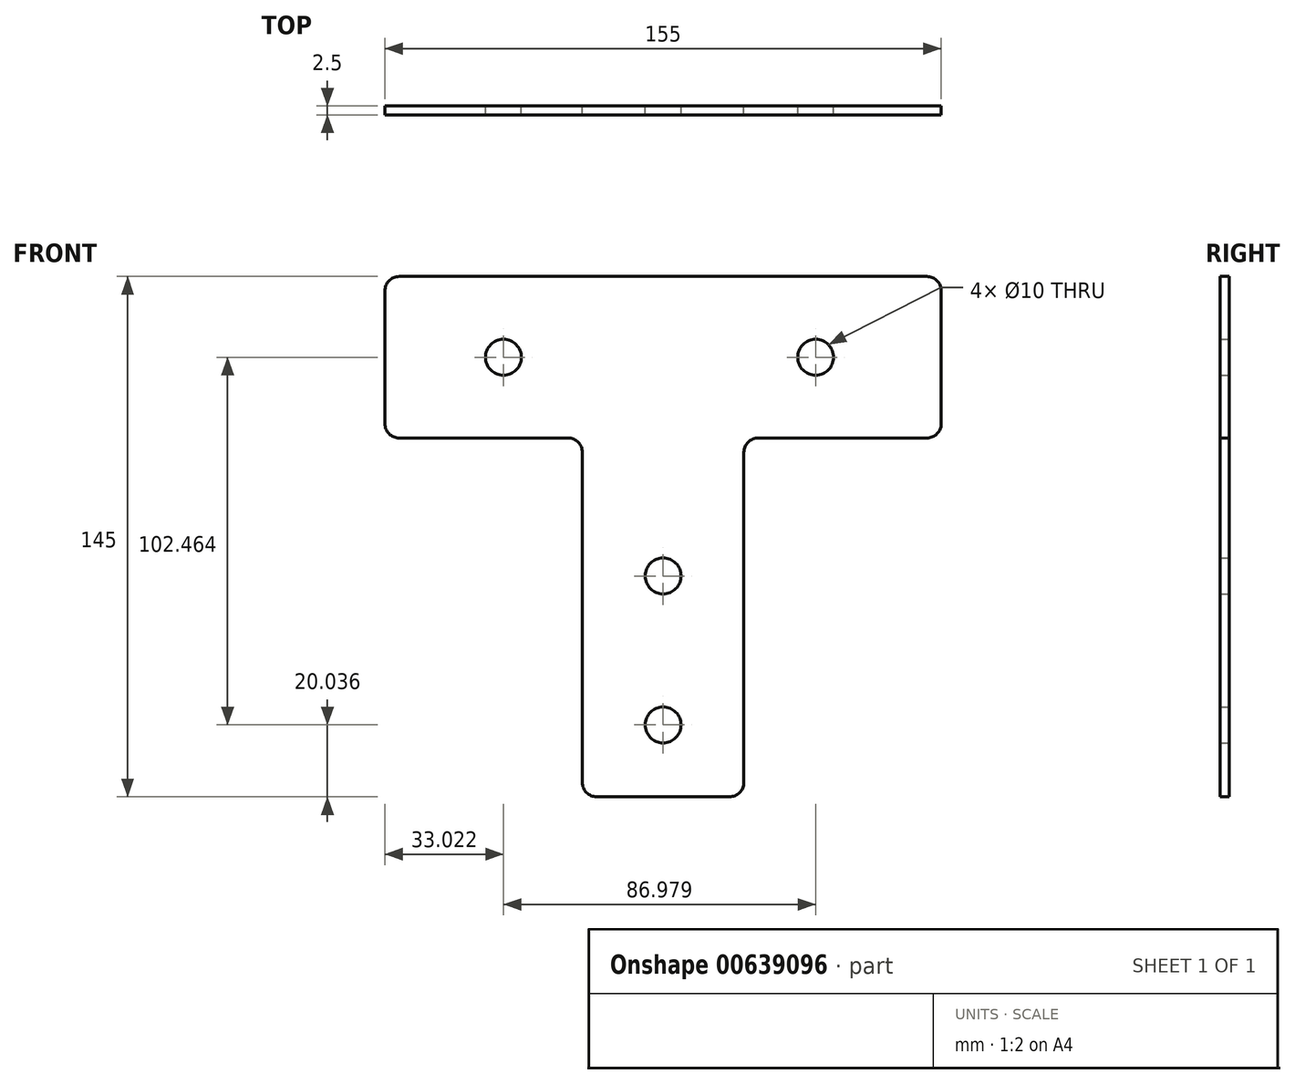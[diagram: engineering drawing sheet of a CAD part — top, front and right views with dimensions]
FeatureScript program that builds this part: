
annotation { "Feature Type Name" : "Feature", "Feature Type Description" : "" }
export const myFeature = defineFeature(function(context is Context, id is Id, definition is map)
    precondition{}
    {
        {
            var Q0;
            Q0=qCreatedBy(makeId("Front.planeOp"),FACE);
            var sketch = newSketch(context, id + "F0", { "sketchPlane" : qUnion([Q0])});
            skLineSegment(sketch, "E0.bottom", {"start": v(73.5, 22.5) * mm, "end": v(-73.5, 22.5) * mm});
            skLineSegment(sketch, "E0.top", {"start": v(77.5, -22.5) * mm, "end": v(22.5, -22.5) * mm});
            skLineSegment(sketch, "E0.left", {"start": v(77.5, 18.5) * mm, "end": v(77.5, -18.5) * mm});
            skLineSegment(sketch, "E0.right", {"start": v(-77.5, 18.5) * mm, "end": v(-77.5, -18.5) * mm});
            skPoint(sketch, "E0.middle", {"position": v(0, 0) * mm});
            skLineSegment(sketch, "E1", {"start": v(73.5, -22.5) * mm, "end": v(26.5, -22.5) * mm});
            skLineSegment(sketch, "E2", {"start": v(22.5, -26.5) * mm, "end": v(22.5, -118.5) * mm});
            skLineSegment(sketch, "E3", {"start": v(18.5, -122.5) * mm, "end": v(-18.5, -122.5) * mm});
            skLineSegment(sketch, "E4", {"start": v(-22.5, -118.5) * mm, "end": v(-22.5, -26.5) * mm});
            skLineSegment(sketch, "E5", {"start": v(-22.5, -22.5) * mm, "end": v(-77.5, -22.5) * mm});
            skLineSegment(sketch, "E6.trimOffspring", {"start": v(-26.5, -22.5) * mm, "end": v(-73.5, -22.5) * mm});
            skPoint(sketch, "E7.visualSharp", {"position": v(-77.5, 22.5) * mm});
            skArc(sketch, "E7.filletArc", {"start": v(-73.5, 22.5) * mm, "mid": v(-76.33, 21.33) * mm, "end": v(-77.5, 18.5) * mm});
            skPoint(sketch, "E8.visualSharp", {"position": v(-77.5, -22.5) * mm});
            skArc(sketch, "E8.filletArc", {"start": v(-77.5, -18.5) * mm, "mid": v(-76.33, -21.33) * mm, "end": v(-73.5, -22.5) * mm});
            skPoint(sketch, "E9.visualSharp", {"position": v(-22.5, -22.5) * mm});
            skArc(sketch, "E9.filletArc", {"start": v(-22.5, -26.5) * mm, "mid": v(-23.67, -23.67) * mm, "end": v(-26.5, -22.5) * mm});
            skPoint(sketch, "E10.visualSharp", {"position": v(-22.5, -122.5) * mm});
            skArc(sketch, "E10.filletArc", {"start": v(-22.5, -118.5) * mm, "mid": v(-21.33, -121.33) * mm, "end": v(-18.5, -122.5) * mm});
            skPoint(sketch, "E11.visualSharp", {"position": v(22.5, -122.5) * mm});
            skArc(sketch, "E11.filletArc", {"start": v(18.5, -122.5) * mm, "mid": v(21.33, -121.33) * mm, "end": v(22.5, -118.5) * mm});
            skPoint(sketch, "E12.visualSharp", {"position": v(22.5, -22.5) * mm});
            skArc(sketch, "E12.filletArc", {"start": v(26.5, -22.5) * mm, "mid": v(23.67, -23.67) * mm, "end": v(22.5, -26.5) * mm});
            skPoint(sketch, "E13.visualSharp", {"position": v(77.5, -22.5) * mm});
            skArc(sketch, "E13.filletArc", {"start": v(73.5, -22.5) * mm, "mid": v(76.33, -21.33) * mm, "end": v(77.5, -18.5) * mm});
            skPoint(sketch, "E14.visualSharp", {"position": v(77.5, 22.5) * mm});
            skArc(sketch, "E14.filletArc", {"start": v(77.5, 18.5) * mm, "mid": v(76.33, 21.33) * mm, "end": v(73.5, 22.5) * mm});
            skSolve(sketch);
        }
        {
            var Q0;
            Q0 = qSketchRegion(id + "F0", true);
            extrude(context, id + "F1", {"entities" : qUnion([Q0]), "depth" : 2.5 * mm, "offsetDistance" : 25 * mm});
        }
        {
            var Q0;
            Q0=qCreatedBy(makeId("Front.planeOp"),FACE);
            var sketch = newSketch(context, id + "F2", { "sketchPlane" : qUnion([Q0])});
            skCircle(sketch, "E15", {"center": v(-44.48, 0) * mm, "radius": 5 * mm});
            skCircle(sketch, "E16", {"center": v(42.5, 0) * mm, "radius": 5 * mm});
            skCircle(sketch, "E17", {"center": v(0, -60.95) * mm, "radius": 5 * mm});
            skCircle(sketch, "E18", {"center": v(0, -102.46) * mm, "radius": 5 * mm});
            skSolve(sketch);
        }
        {
            var Q0;
            Q0 = qSketchRegion(id + "F2", true);
            extrude(context, id + "F3", {"entities" : qUnion([Q0]), "operationType" : NewBodyOperationType.REMOVE, "endBound" : BoundingType.THROUGH_ALL, "depth" : 25 * mm, "offsetDistance" : 25 * mm});
        }
    });
